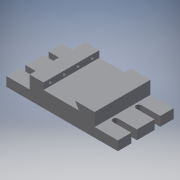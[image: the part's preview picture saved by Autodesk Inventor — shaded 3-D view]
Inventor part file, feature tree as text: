
AUTODESK INVENTOR PART (.ipt)
format: ipt  version: 2016 (Build 200138000, 138)  size: 189,952 bytes
history: native  units: mm
features: projected_geometry x5, extrude x4, sketch x4, hole x1
ambient origin geometry x8: Origin, YZ Plane, XZ Plane, XY Plane, X Axis, Y Axis, Z Axis, Center Point
bodies: Solid1 (feature_tree)
feature tree (14):
  extrude  "Extrusion1"  Depth=60.0mm
  extrude  "Extrusion2"  TaperAngle=60.0deg  [1 undecoded]
  extrude  "Extrusion7"  Depth=7.0mm TaperAngle=0.0deg
  extrude  "Extrusion8"  Depth=15.0mm
  hole  "Hole3"  [1 undecoded]
  sketch  "Sketch1"  dims[d0=120.0mm d1=60.0mm]
  sketch  "Sketch9"  dims[d2=24.0mm d3=0.0mm d5=60.0deg]
  projected_geometry  "Projected Loop13"
  projected_geometry  "Projected Loop14"
  sketch  "Sketch10"  dims[d7=7.0mm d9=16.5mm d10=0.0mm]
  projected_geometry  "Projected Loop15"
  projected_geometry  "Projected Loop16"
  sketch  "Sketch11"  dims[d37=1.0mm d39=17.464mm d40=60.0deg d64=20.0mm d65=25.0mm d66=25.0mm d67=25.0mm d68=25.0mm d69=25.0mm d70=25.0mm d71=14.0mm d72=0.0mm d73=12.5mm d74=12.5mm d75=6.0mm d76=20.0mm d77=6.0mm d78=20.0mm d79=6.0mm d80=20.0mm d81=6.0mm d82=20.0mm d83=20.0mm d84=0.0mm d85=3.5mm d86=7.5mm d87=15.0mm d88=15.0mm d89=15.0mm d90=3.242mm d91=8.0mm d92=4.0mm d93=2.0mm d94=90.0deg d95=11.8mm d96=20.594885mm]
  projected_geometry  "Projected Loop17"
note: 2 required parameter values undecoded (feature->parameter linkage not recoverable at this tier; creation-order binding heuristic only, values carry confidence <= 0.55)
